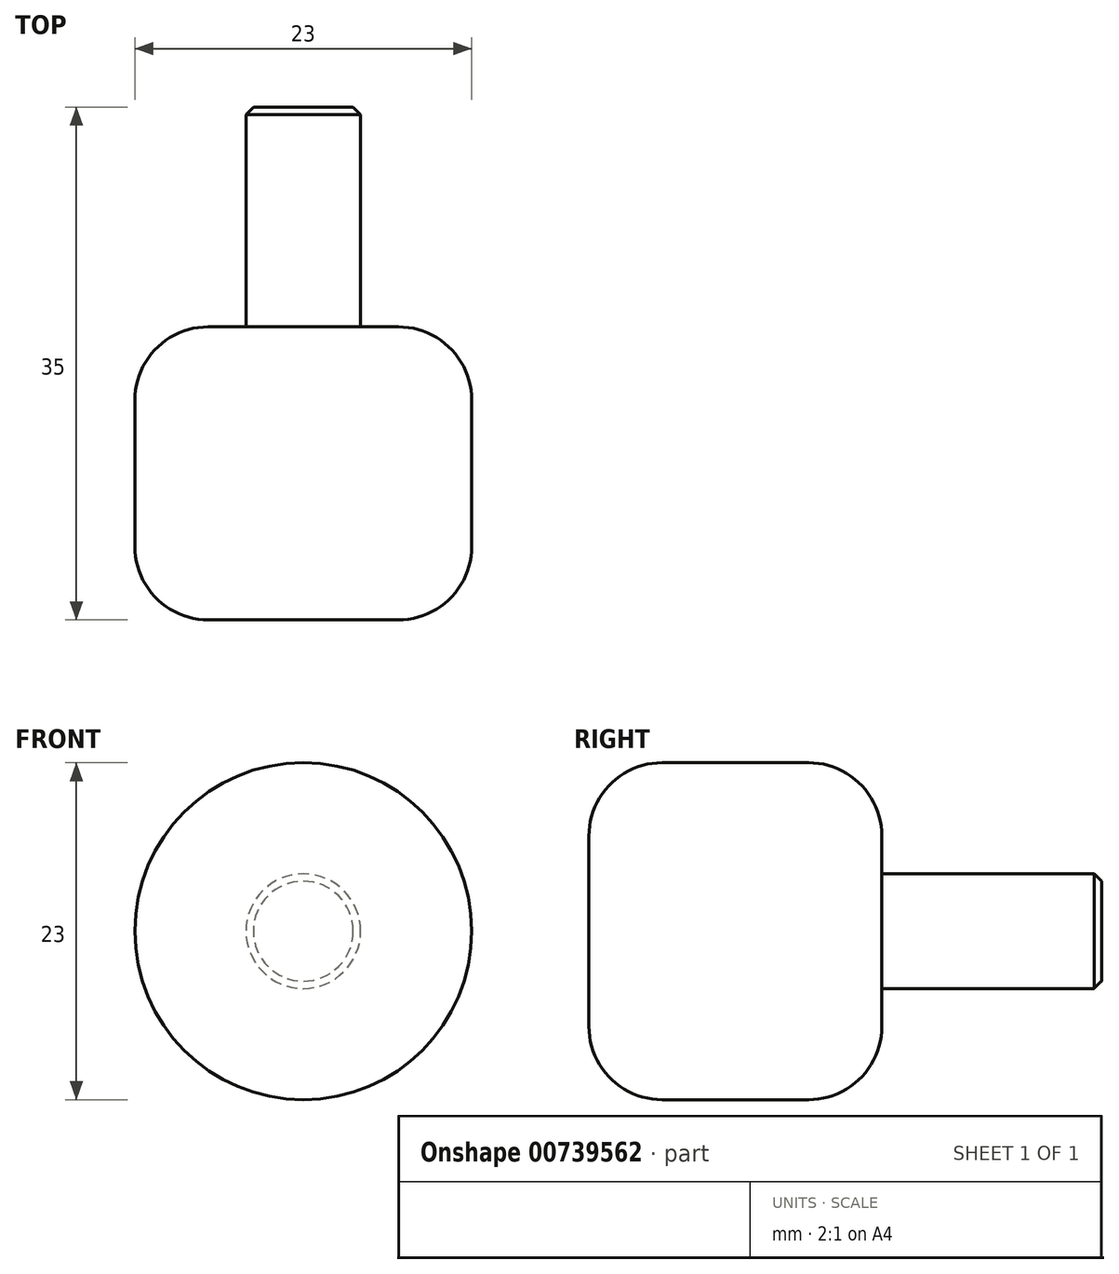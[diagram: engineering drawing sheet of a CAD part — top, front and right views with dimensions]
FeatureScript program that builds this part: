
annotation { "Feature Type Name" : "Feature", "Feature Type Description" : "" }
export const myFeature = defineFeature(function(context is Context, id is Id, definition is map)
    precondition{}
    {
        {
            var Q0;
            Q0=qCreatedBy(makeId("Front.planeOp"),FACE);
            var sketch = newSketch(context, id + "F0", { "sketchPlane" : qUnion([Q0])});
            skCircle(sketch, "E0", {"center": v(0, 0) * mm, "radius": 11.5 * mm});
            skSolve(sketch);
        }
        {
            var Q0;
            Q0 = qSketchRegion(id + "F0", true);
            extrude(context, id + "F1", {"entities" : qUnion([Q0]), "depth" : 20 * mm, "offsetDistance" : 25 * mm});
        }
        {
            var Q0;
            Q0=makeQuery(id+"F1.opExtrude","CAP_EDGE",EDGE,{"disambiguationData":[OSD([sQuery(id+"F0.wireOp",EDGE,"E0")])],"isStart":false});
            var Q1;
            Q1=makeQuery(id+"F1.opExtrude","CAP_EDGE",EDGE,{"disambiguationData":[OSD([sQuery(id+"F0.wireOp",EDGE,"E0")])],"isStart":true});
            fillet(context, id + "F2", {"entities" : qUnion([Q0, Q1]), "radius" : 5 * mm, "tangentPropagation" : true, "allowEdgeOverflow" : false});
        }
        {
            var Q0;
            Q0=qCreatedBy(makeId("Front.planeOp"),FACE);
            var sketch = newSketch(context, id + "F3", { "sketchPlane" : qUnion([Q0])});
            skCircle(sketch, "E1", {"center": v(0, 0) * mm, "radius": 3.91 * mm});
            skSolve(sketch);
        }
        {
            var Q0;
            Q0 = qSketchRegion(id + "F3", true);
            extrude(context, id + "F4", {"entities" : qUnion([Q0]), "operationType" : NewBodyOperationType.ADD, "oppositeDirection" : true, "depth" : 15 * mm, "offsetDistance" : 25 * mm});
        }
        {
            var Q0;
            Q0=makeQuery(id+"F4.opExtrude","CAP_EDGE",EDGE,{"disambiguationData":[OSD([sQuery(id+"F3.wireOp",EDGE,"E1")])],"isStart":false});
            chamfer(context, id + "F5", {"entities" : qUnion([Q0]), "width" : 0.5 * mm, "tangentPropagation" : true});
        }
    });
